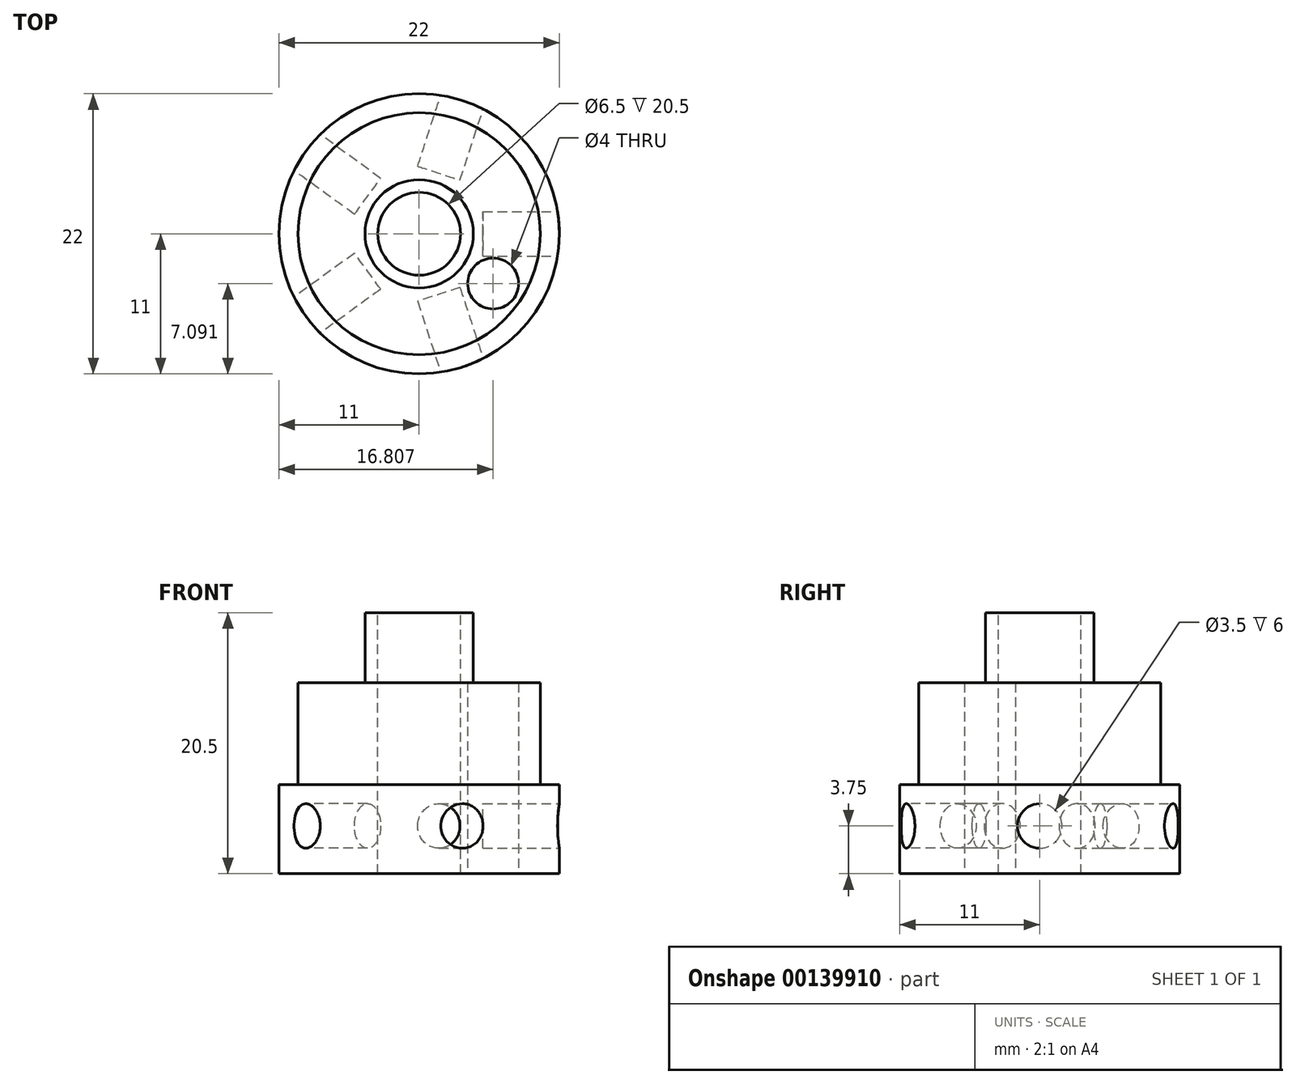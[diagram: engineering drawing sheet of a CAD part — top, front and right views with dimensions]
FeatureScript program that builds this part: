
annotation { "Feature Type Name" : "Feature", "Feature Type Description" : "" }
export const myFeature = defineFeature(function(context is Context, id is Id, definition is map)
    precondition{}
    {
        {
            var Q0;
            Q0=qCreatedBy(makeId("Top.planeOp"),FACE);
            var sketch = newSketch(context, id + "F0", { "sketchPlane" : qUnion([Q0])});
            skCircle(sketch, "E0", {"center": v(0, 0) * mm, "radius": 11 * mm});
            skSolve(sketch);
        }
        {
            var Q0;
            Q0 = qSketchRegion(id + "F0", true);
            extrude(context, id + "F1", {"entities" : qUnion([Q0]), "depth" : 7 * mm});
        }
        {
            var Q0;
            Q0=makeQuery(id+"F1.opExtrude","CAP_FACE",FACE,{"disambiguationData":[OSD([sQuery(id+"F0.wireOp",EDGE,"E0")])],"isStart":false});
            var sketch = newSketch(context, id + "F2", { "sketchPlane" : qUnion([Q0])});
            skCircle(sketch, "E1", {"center": v(0, 0) * mm, "radius": 9.5 * mm});
            skSolve(sketch);
        }
        {
            var Q0;
            Q0 = qSketchRegion(id + "F2", true);
            extrude(context, id + "F3", {"entities" : qUnion([Q0]), "operationType" : NewBodyOperationType.ADD, "depth" : 8 * mm});
        }
        {
            var Q0;
            Q0=makeQuery(id+"F3.opExtrude","CAP_FACE",FACE,{"disambiguationData":[OSD([sQuery(id+"F2.wireOp",EDGE,"E1")])],"isStart":false});
            var sketch = newSketch(context, id + "F4", { "sketchPlane" : qUnion([Q0])});
            skCircle(sketch, "E2", {"center": v(0, 0) * mm, "radius": 4.25 * mm});
            skSolve(sketch);
        }
        {
            var Q0;
            Q0 = qSketchRegion(id + "F4", true);
            extrude(context, id + "F5", {"entities" : qUnion([Q0]), "operationType" : NewBodyOperationType.ADD, "depth" : 5.5 * mm});
        }
        {
            var Q0;
            Q0=makeQuery(id+"F5.opExtrude","CAP_FACE",FACE,{"disambiguationData":[OSD([sQuery(id+"F4.wireOp",EDGE,"E2")])],"isStart":false});
            var sketch = newSketch(context, id + "F6", { "sketchPlane" : qUnion([Q0])});
            skCircle(sketch, "E3", {"center": v(0, 0) * mm, "radius": 3.25 * mm});
            skSolve(sketch);
        }
        {
            var Q0;
            Q0 = qSketchRegion(id + "F6", true);
            extrude(context, id + "F7", {"entities" : qUnion([Q0]), "operationType" : NewBodyOperationType.REMOVE, "endBound" : BoundingType.THROUGH_ALL, "oppositeDirection" : true, "depth" : 25 * mm});
        }
        {
            var Q0;
            Q0=makeQuery(id+"F1.opExtrude","CAP_FACE",FACE,{"disambiguationData":[OSD([sQuery(id+"F0.wireOp",EDGE,"E0")])],"isStart":true});
            var sketch = newSketch(context, id + "F8", { "sketchPlane" : qUnion([Q0])});
            skLineSegment(sketch, "E4", {"start": v(0, 0) * mm, "end": v(11, 0) * mm, "construction": true});
            skLineSegment(sketch, "E5", {"start": v(0, 0) * mm, "end": v(3.4, 10.46) * mm, "construction": true});
            skLineSegment(sketch, "E6", {"start": v(0, 0) * mm, "end": v(-8.9, 6.47) * mm, "construction": true});
            skLineSegment(sketch, "E7", {"start": v(0, 0) * mm, "end": v(-8.9, -6.47) * mm, "construction": true});
            skLineSegment(sketch, "E8", {"start": v(0, 0) * mm, "end": v(3.4, -10.46) * mm, "construction": true});
            skLineSegment(sketch, "E9", {"start": v(11, 3.63) * mm, "end": v(11, -3.46) * mm, "construction": true});
            skLineSegment(sketch, "E10", {"start": v(3.4, 10.46) * mm, "end": v(0.34, 11.46) * mm, "construction": true});
            skLineSegment(sketch, "E11", {"start": v(3.4, 10.46) * mm, "end": v(7.1, 9.26) * mm, "construction": true});
            skLineSegment(sketch, "E12", {"start": v(-8.9, 6.47) * mm, "end": v(-6.72, 9.46) * mm, "construction": true});
            skLineSegment(sketch, "E13", {"start": v(-8.9, -6.47) * mm, "end": v(-11, -3.57) * mm, "construction": true});
            skLineSegment(sketch, "E14", {"start": v(3.4, -10.46) * mm, "end": v(7.2, -9.23) * mm, "construction": true});
            skSolve(sketch);
        }
        {
            var Q0;
            Q0=sQuery(id+"F8.wireOp",EDGE,"E9");
            cPlane(context, id + "F9", {"entities" : qUnion([Q0]), "cplaneType" : CPlaneType.LINE_ANGLE, "offset" : 25 * mm, "angle" : 90 * degree, "width" : 150 * mm, "height" : 150 * mm});
        }
        {
            var Q0;
            Q0=qCreatedBy(id+"F9.planeOp",FACE);
            var sketch = newSketch(context, id + "F10", { "sketchPlane" : qUnion([Q0])});
            skCircle(sketch, "E15", {"center": v(0, 3.75) * mm, "radius": 1.75 * mm});
            skSolve(sketch);
        }
        {
            var Q0;
            Q0=sQuery(id+"F8.wireOp",EDGE,"E11");
            cPlane(context, id + "F11", {"entities" : qUnion([Q0]), "cplaneType" : CPlaneType.LINE_ANGLE, "offset" : 25 * mm, "angle" : 0 * degree, "width" : 150 * mm, "height" : 150 * mm});
        }
        {
            var Q0;
            Q0=qCreatedBy(id+"F11.planeOp",FACE);
            var sketch = newSketch(context, id + "F12", { "sketchPlane" : qUnion([Q0])});
            skCircle(sketch, "E16", {"center": v(0, 3.75) * mm, "radius": 1.75 * mm});
            skSolve(sketch);
        }
        {
            var Q0;
            Q0=sQuery(id+"F8.wireOp",EDGE,"E12");
            cPlane(context, id + "F13", {"entities" : qUnion([Q0]), "cplaneType" : CPlaneType.LINE_ANGLE, "offset" : 25 * mm, "angle" : 90 * degree, "width" : 150 * mm, "height" : 150 * mm});
        }
        {
            var Q0;
            Q0=qCreatedBy(id+"F13.planeOp",FACE);
            var sketch = newSketch(context, id + "F14", { "sketchPlane" : qUnion([Q0])});
            skCircle(sketch, "E17", {"center": v(0, 3.75) * mm, "radius": 1.75 * mm});
            skSolve(sketch);
        }
        {
            var Q0;
            Q0=sQuery(id+"F8.wireOp",EDGE,"E13");
            cPlane(context, id + "F15", {"entities" : qUnion([Q0]), "cplaneType" : CPlaneType.LINE_ANGLE, "offset" : 25 * mm, "angle" : 90 * degree, "width" : 150 * mm, "height" : 150 * mm});
        }
        {
            var Q0;
            Q0=qCreatedBy(id+"F15.planeOp",FACE);
            var sketch = newSketch(context, id + "F16", { "sketchPlane" : qUnion([Q0])});
            skCircle(sketch, "E18", {"center": v(0, 3.75) * mm, "radius": 1.75 * mm});
            skSolve(sketch);
        }
        {
            var Q0;
            Q0=sQuery(id+"F8.wireOp",EDGE,"E14");
            cPlane(context, id + "F17", {"entities" : qUnion([Q0]), "cplaneType" : CPlaneType.LINE_ANGLE, "offset" : 25 * mm, "angle" : 0 * degree, "width" : 150 * mm, "height" : 150 * mm});
        }
        {
            var Q0;
            Q0=qCreatedBy(id+"F17.planeOp",FACE);
            var sketch = newSketch(context, id + "F18", { "sketchPlane" : qUnion([Q0])});
            skCircle(sketch, "E19", {"center": v(0, 3.75) * mm, "radius": 1.75 * mm});
            skSolve(sketch);
        }
        {
            var Q0;
            Q0=makeQuery(id+"F10.imprint","IMPRINT",FACE,{"disambiguationData":[TD([[makeQuery(id+"F10.imprint","IMPRINT",EDGE,{"derivedFrom":sQuery(id+"F10.wireOp",EDGE,"E15")}),1.0]])]});
            extrude(context, id + "F19", {"entities" : qUnion([Q0]), "operationType" : NewBodyOperationType.REMOVE, "oppositeDirection" : true, "depth" : 6 * mm});
        }
        {
            var Q0;
            Q0=makeQuery(id+"F12.imprint","IMPRINT",FACE,{"disambiguationData":[TD([[makeQuery(id+"F12.imprint","IMPRINT",EDGE,{"derivedFrom":sQuery(id+"F12.wireOp",EDGE,"E16")}),1.0]])]});
            extrude(context, id + "F20", {"entities" : qUnion([Q0]), "operationType" : NewBodyOperationType.REMOVE, "depth" : 6 * mm});
        }
        {
            var Q0;
            Q0=makeQuery(id+"F14.imprint","IMPRINT",FACE,{"disambiguationData":[TD([[makeQuery(id+"F14.imprint","IMPRINT",EDGE,{"derivedFrom":sQuery(id+"F14.wireOp",EDGE,"E17")}),1.0]])]});
            extrude(context, id + "F21", {"entities" : qUnion([Q0]), "operationType" : NewBodyOperationType.REMOVE, "depth" : 6 * mm});
        }
        {
            var Q0;
            Q0=makeQuery(id+"F16.imprint","IMPRINT",FACE,{"disambiguationData":[TD([[makeQuery(id+"F16.imprint","IMPRINT",EDGE,{"derivedFrom":sQuery(id+"F16.wireOp",EDGE,"E18")}),1.0]])]});
            extrude(context, id + "F22", {"entities" : qUnion([Q0]), "operationType" : NewBodyOperationType.REMOVE, "depth" : 6 * mm});
        }
        {
            var Q0;
            Q0=makeQuery(id+"F18.imprint","IMPRINT",FACE,{"disambiguationData":[TD([[makeQuery(id+"F18.imprint","IMPRINT",EDGE,{"derivedFrom":sQuery(id+"F18.wireOp",EDGE,"E19")}),1.0]])]});
            extrude(context, id + "F23", {"entities" : qUnion([Q0]), "operationType" : NewBodyOperationType.REMOVE, "oppositeDirection" : true, "depth" : 6 * mm});
        }
        {
            var Q0;
            {var subQ0=sQuery(id+"F0.wireOp",EDGE,"E0");Q0=makeQuery(id+"F8.imprint","IMPRINT",FACE,{"disambiguationData":[TD([[makeQuery(id+"F8.imprint","IMPRINT",EDGE,{"derivedFrom":makeQuery(id+"F1.opExtrude","CAP_EDGE",EDGE,{"disambiguationData":[OSD([subQ0])],"isStart":true})}),-1.0]])]});}
            var sketch = newSketch(context, id + "F24", { "sketchPlane" : qUnion([Q0])});
            skPoint(sketch, "E20.0", {"position": v(11, 0) * mm});
            skLineSegment(sketch, "E21", {"start": v(11, 0) * mm, "end": v(5.8, 3.9) * mm, "construction": true});
            skCircle(sketch, "E22", {"center": v(5.8, 3.9) * mm, "radius": 2 * mm});
            skLineSegment(sketch, "E23", {"start": v(0, 0) * mm, "end": v(5.8, 3.9) * mm, "construction": true});
            skSolve(sketch);
        }
        {
            var Q0;
            Q0 = qSketchRegion(id + "F24", true);
            extrude(context, id + "F25", {"entities" : qUnion([Q0]), "operationType" : NewBodyOperationType.REMOVE, "oppositeDirection" : true, "depth" : 25 * mm});
        }
    });
